# Revit family: GHR
name_source: partatom
category: Air Terminals
revit_build: Autodesk Revit MEP 2012 (Build: 20110309_2315(x64)
units: mm (PartAtom-declared; Revit-internal decimal feet)

## types (4) — shared parameters
Alto aleta = 11/32"
Ancho aleta = 1/2"
Ancho barra = 1/16"
Largo barra = 15/64"
Manufacturer = INNES
Máxima presión estática = 0.00 in-wg
Máxima velocidad de cuello = 0 FPM
Mínima presión estática = 0.00 in-wg
Mínima velocidad de cuello = 0 FPM
Separacion = 9/32"
Separacion 1 = 29/32"
URL = http://www.innes.com.mx

## per-type parameters (varying)
| type | Ancho A | Largo B | Medida horizontal A | Medida vertical B | No. de elementos | No. de elementos 1 | Separacion barras |
| GHR-12 | 11 11/16" | 11 9/16" | 13 13/16" | 13 11/16" | 41 | 12 | 10 5/8" |
| GHR-13 | 12 11/16" | 12 9/16" | 14 13/16" | 14 11/16" | 45 | 13 | 11 5/8" |
| GHR-14 | 13 11/16" | 13 9/16" | 15 13/16" | 15 11/16" | 48 | 14 | 12 5/8" |
| GHR-15 | 14 11/16" | 14 9/16" | 16 13/16" | 16 11/16" | 52 | 15 | 13 5/8" |

## geometry (parser evidence)
native form markers: Sweep x4
no freeform markers — native parametric forms only
